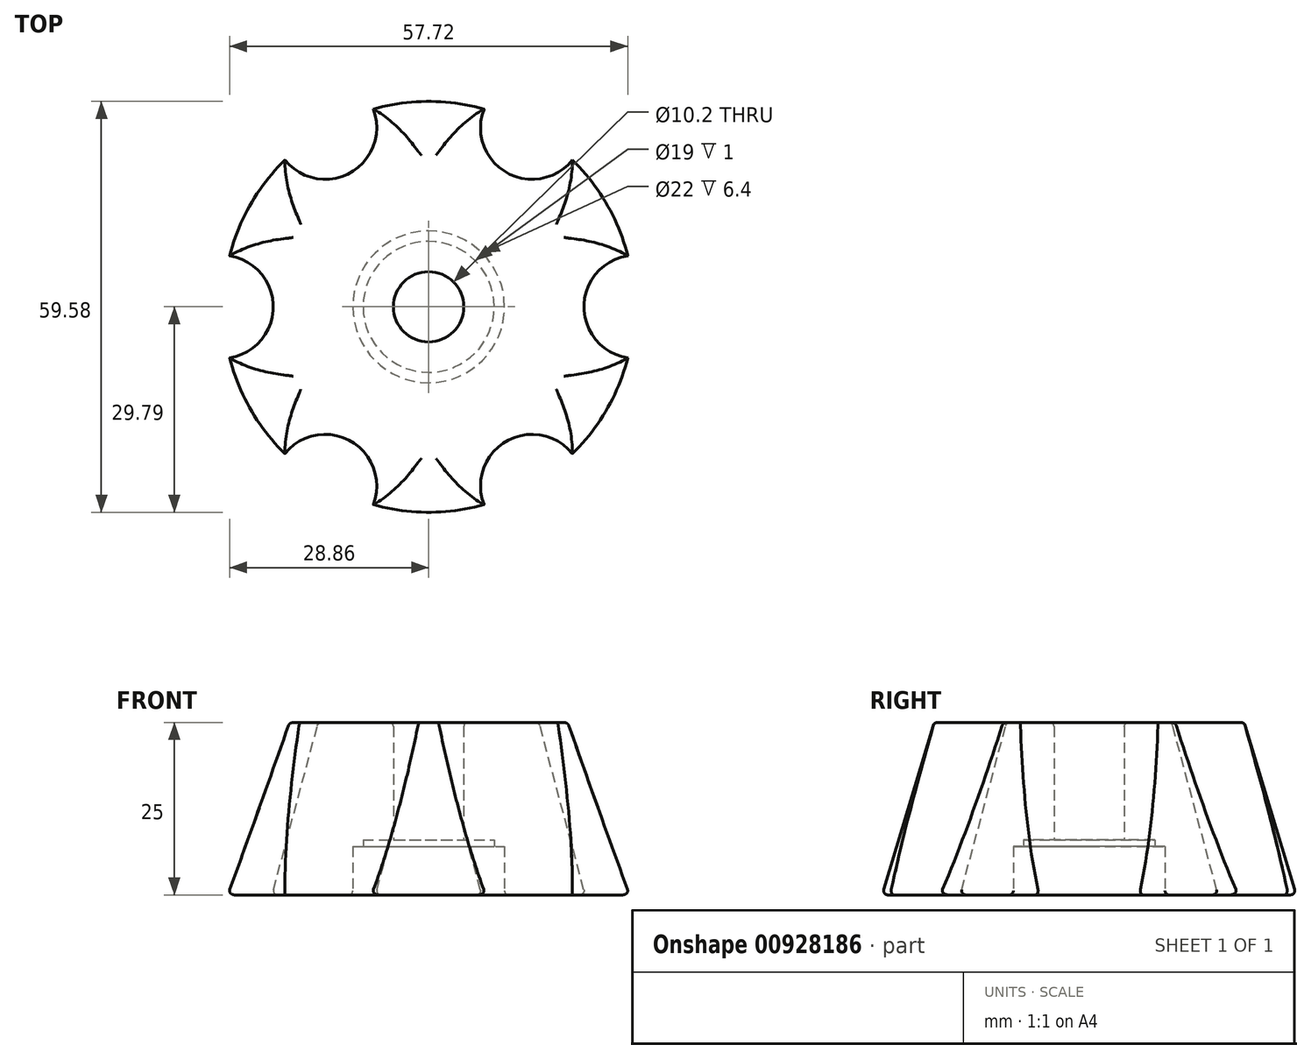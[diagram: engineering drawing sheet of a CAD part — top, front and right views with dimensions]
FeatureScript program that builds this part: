
annotation { "Feature Type Name" : "Feature", "Feature Type Description" : "" }
export const myFeature = defineFeature(function(context is Context, id is Id, definition is map)
    precondition{}
    {
        {
            var Q0;
            Q0=qCreatedBy(makeId("Front.planeOp"),FACE);
            var sketch = newSketch(context, id + "F0", { "sketchPlane" : qUnion([Q0])});
            skLineSegment(sketch, "E0", {"start": v(0, 0) * mm, "end": v(0, 86.98) * mm, "construction": true});
            skLineSegment(sketch, "E1", {"start": v(5.1, 25) * mm, "end": v(5.1, 8) * mm});
            skLineSegment(sketch, "E2", {"start": v(5.1, 8) * mm, "end": v(9.5, 8) * mm});
            skLineSegment(sketch, "E3", {"start": v(9.5, 8) * mm, "end": v(9.5, 7) * mm});
            skLineSegment(sketch, "E4", {"start": v(9.5, 7) * mm, "end": v(11, 7) * mm});
            skLineSegment(sketch, "E5", {"start": v(11, 7) * mm, "end": v(11, 0) * mm});
            skLineSegment(sketch, "E6", {"start": v(11, 0) * mm, "end": v(30, 0) * mm});
            skLineSegment(sketch, "E7", {"start": v(30, 0) * mm, "end": v(22.5, 25) * mm});
            skLineSegment(sketch, "E8", {"start": v(22.5, 25) * mm, "end": v(5.1, 25) * mm});
            skSolve(sketch);
        }
        {
            var Q0;
            Q0 = qSketchRegion(id + "F0", true);
            var Q1;
            Q1=sQuery(id+"F0.wireOp",EDGE,"E0");
            revolve(context, id + "F1", {"surfaceOperationType" : NewSurfaceOperationType.NEW, "entities" : qUnion([Q0]), "axis" : qUnion([Q1]), "revolveType" : RevolveType.FULL});
        }
        {
            var Q0;
            Q0=makeQuery(id+"F1.opRevolve","SWEPT_FACE",FACE,{"disambiguationData":[OSD([sQuery(id+"F0.wireOp",EDGE,"E8")])]});
            var sketch = newSketch(context, id + "F2", { "sketchPlane" : qUnion([Q0])});
            skLineSegment(sketch, "E9", {"start": v(0, 0) * mm, "end": v(-48.07, 0) * mm, "construction": true});
            skCircle(sketch, "E10", {"center": v(-30, 0) * mm, "radius": 14 * mm});
            skCircle(sketch, "E11.0", {"center": v(0, 0) * mm, "radius": 30 * mm, "construction": true});
            skCircle(sketch, "E12.1.0", {"center": v(-15, -25.98) * mm, "radius": 14 * mm});
            skCircle(sketch, "E12.2.0", {"center": v(15, -25.98) * mm, "radius": 14 * mm});
            skCircle(sketch, "E12.3.0", {"center": v(30, 0) * mm, "radius": 14 * mm});
            skCircle(sketch, "E12.4.0", {"center": v(15, 25.98) * mm, "radius": 14 * mm});
            skCircle(sketch, "E12.5.0", {"center": v(-15, 25.98) * mm, "radius": 14 * mm});
            skSolve(sketch);
        }
        {
            var Q0;
            Q0 = qSketchRegion(id + "F2", true);
            var Q1;
            Q1=sQuery(id+"F2.wireOp",EDGE,"E10");
            extrude(context, id + "F3", {"entities" : qUnion([Q0]), "operationType" : NewBodyOperationType.REMOVE, "surfaceEntities" : qUnion([Q1]), "endBound" : BoundingType.THROUGH_ALL, "oppositeDirection" : true, "depth" : 25 * mm, "offsetDistance" : 25 * mm, "hasDraft" : true, "draftAngle" : 15 * degree, "draftPullDirection" : true});
        }
        {
            var Q0;
            Q0=makeQuery(id+"F1.opRevolve","SWEPT_FACE",FACE,{"disambiguationData":[OSD([sQuery(id+"F0.wireOp",EDGE,"E6")])]});
            var Q1;
            Q1=makeQuery(id+"F1.opRevolve","SWEPT_FACE",FACE,{"disambiguationData":[OSD([sQuery(id+"F0.wireOp",EDGE,"E8")])]});
            fillet(context, id + "F4", {"entities" : qUnion([Q0, Q1]), "radius" : .6 * mm, "tangentPropagation" : true, "allowEdgeOverflow" : false});
        }
    });
